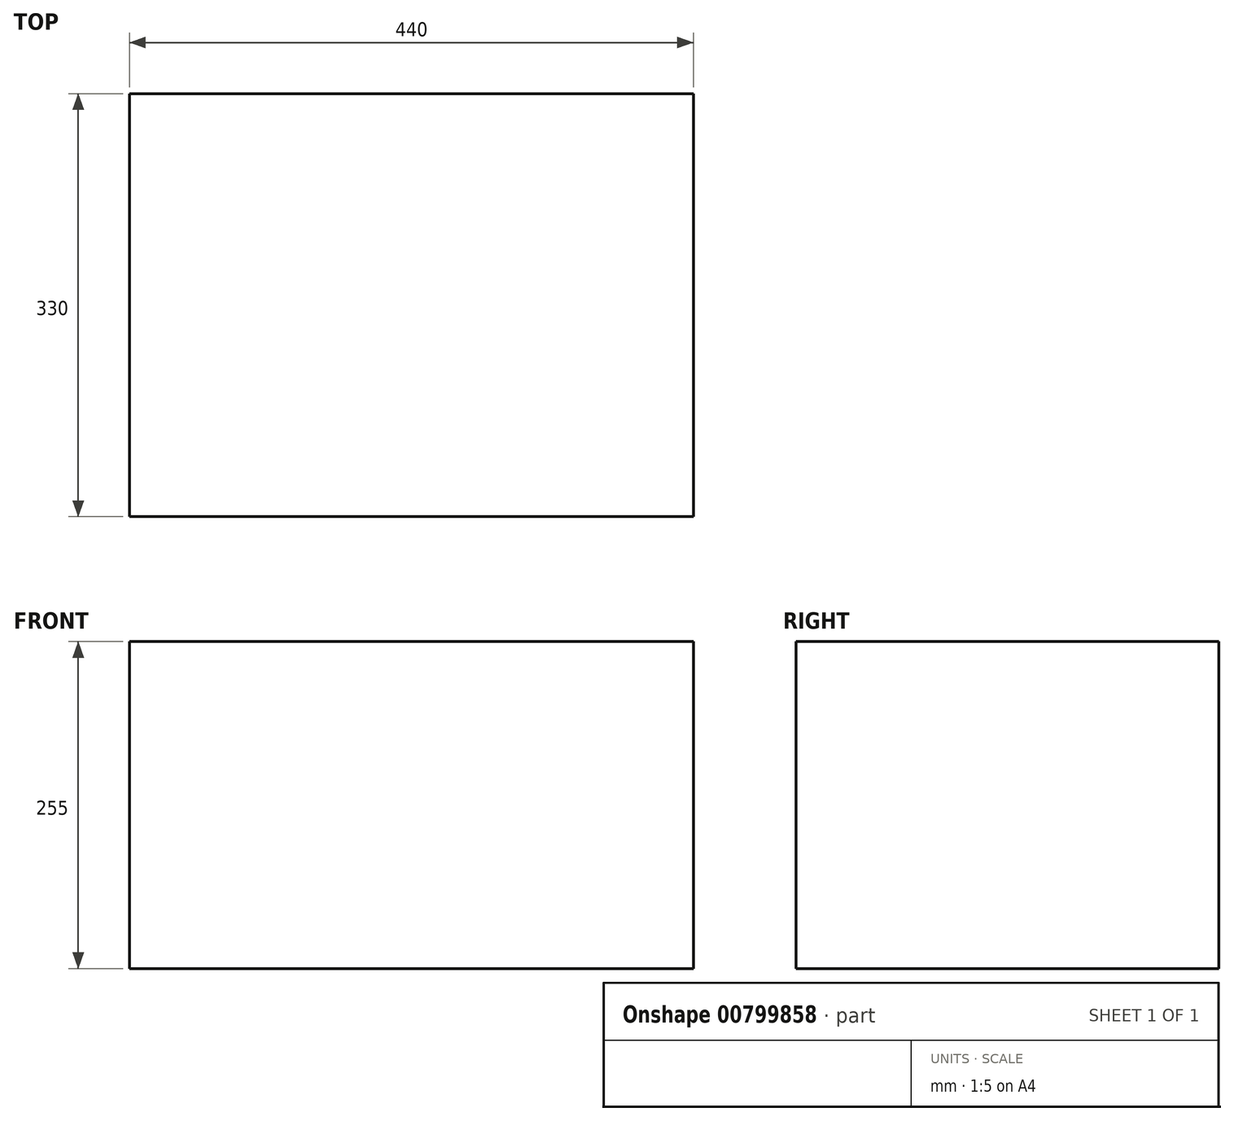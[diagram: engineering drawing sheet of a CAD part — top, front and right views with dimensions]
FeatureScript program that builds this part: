
annotation { "Feature Type Name" : "Feature", "Feature Type Description" : "" }
export const myFeature = defineFeature(function(context is Context, id is Id, definition is map)
    precondition{}
    {
        {
            var Q0;
            Q0=qCreatedBy(makeId("Front.planeOp"),FACE);
            var sketch = newSketch(context, id + "F0", { "sketchPlane" : qUnion([Q0])});
            skLineSegment(sketch, "E0.bottom", {"start": v(220, -127.5) * mm, "end": v(-220, -127.5) * mm});
            skLineSegment(sketch, "E0.top", {"start": v(220, 127.5) * mm, "end": v(-220, 127.5) * mm});
            skLineSegment(sketch, "E0.left", {"start": v(220, -127.5) * mm, "end": v(220, 127.5) * mm});
            skLineSegment(sketch, "E0.right", {"start": v(-220, -127.5) * mm, "end": v(-220, 127.5) * mm});
            skPoint(sketch, "E0.middle", {"position": v(0, 0) * mm});
            skSolve(sketch);
        }
        {
            var Q0;
            Q0=makeQuery(id+"F0.imprint","IMPRINT",FACE,{"disambiguationData":[TD([[makeQuery(id+"F0.imprint","IMPRINT",EDGE,{"derivedFrom":sQuery(id+"F0.wireOp",EDGE,"E0.bottom")}),-1.0]])]});
            extrude(context, id + "F1", {"entities" : qUnion([Q0]), "depth" : 330 * mm, "offsetDistance" : 25 * mm});
        }
    });
